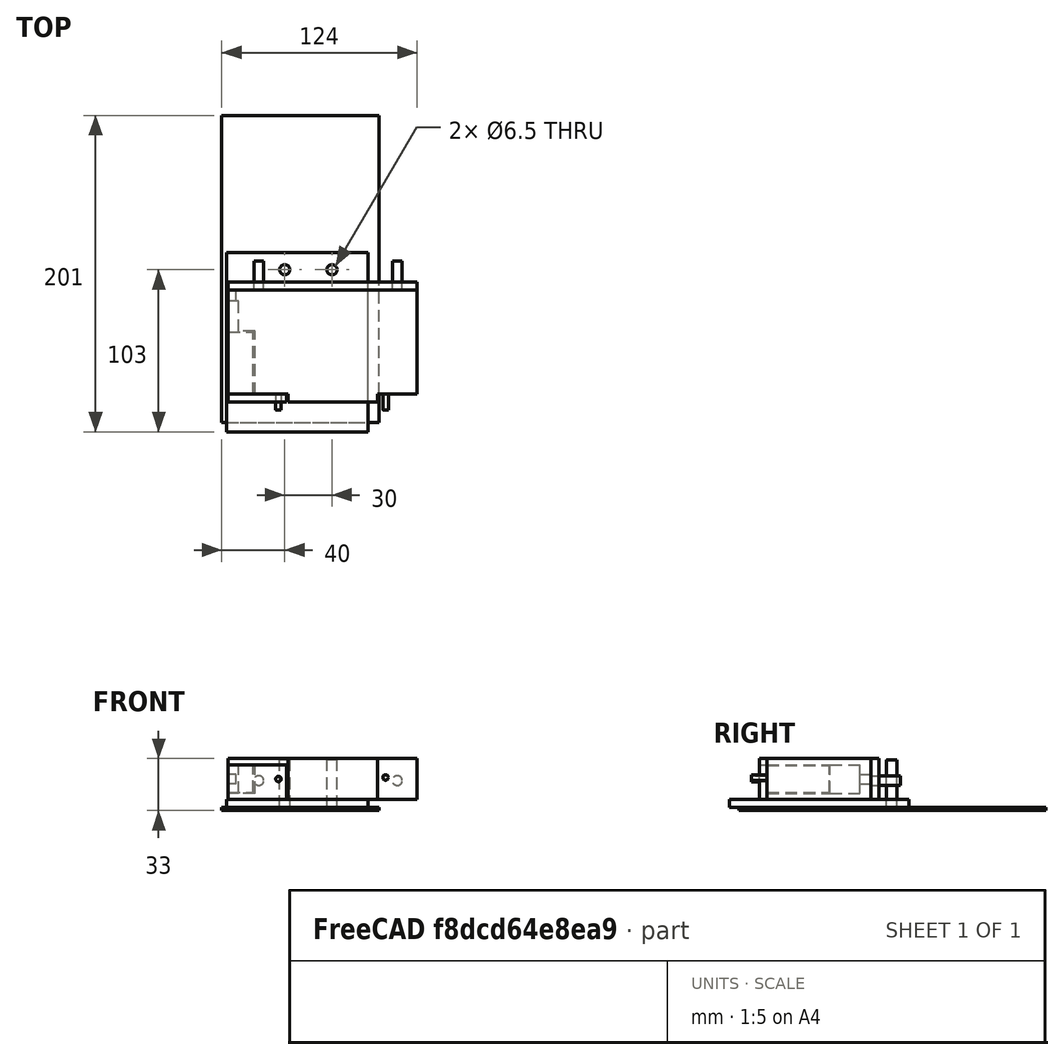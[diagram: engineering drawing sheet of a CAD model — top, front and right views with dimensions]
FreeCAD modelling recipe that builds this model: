
FCSTD DOCUMENT  (FreeCAD 0.18R4 (GitTag))
Label: BreakerHolder
License: All rights reserved
LicenseURL: http://en.wikipedia.org/wiki/All_rights_reserved
objects: Part::Box×10, Part::Cylinder×8, Part::Cut×3, Part::MultiFuse×3
note: 24 computed .brp shape members not serialized (recipe doc carries the construction recipe); baked Part::Feature solids carry a one-line shape summary decoded from their .brp

FEATURE [Part::Box] Box  label="Wall"
  AttacherType = Attacher::AttachEngine3D
  Height = 2
  Length = 100
  Width = 195
FEATURE [Part::Cylinder] Cylinder  label="ScrewHole0"
  Angle = 360
  AttacherType = Attacher::AttachEngine3D
  Height = 10
  Placement = pos=(70,97,-4) rot=(0,0,1;0rad)
  Radius = 3.25
FEATURE [Part::Cylinder] Cylinder001  label="ScrewHole1"
  Angle = 360
  AttacherType = Attacher::AttachEngine3D
  Height = 10
  Placement = pos=(40,97,-3) rot=(0,0,1;0rad)
  Radius = 3.25
FEATURE [Part::Cut] Cut
  Base = -> Box
  Tool = -> Cylinder
FEATURE [Part::Cut] Cut001  label="Wall001"
  Base = -> Cut
  Placement = pos=(154,0,-29) rot=(0,0,1;0rad)
  Tool = -> Cylinder001
FEATURE [Part::Box] Box001  label="Cube"
  AttacherType = Attacher::AttachEngine3D
  Height = 26
  Length = 66
  Width = 120
FEATURE [Part::Cylinder] Cylinder002  label="Cylinder"
  Angle = 360
  AttacherType = Attacher::AttachEngine3D
  Height = 18.5
  Placement = pos=(66,12.5,12) rot=(0,-1,0;4.71239rad)
  Radius = 3.125
FEATURE [Part::Cylinder] Cylinder003  label="Cylinder001"
  Angle = 360
  AttacherType = Attacher::AttachEngine3D
  Height = 18.5
  Placement = pos=(66,100.5,12) rot=(0,1,0;1.5708rad)
  Radius = 3.125
FEATURE [Part::Box] Box002  label="Cube001"
  AttacherType = Attacher::AttachEngine3D
  Height = 26
  Length = 5.6
  Placement = pos=(-5,25,0) rot=(0,0,1;0rad)
  Width = 57
FEATURE [Part::Box] Box003  label="Cube002"
  AttacherType = Attacher::AttachEngine3D
  Height = 6
  Length = 7
  Placement = pos=(59,115,10) rot=(0,0,1;0rad)
  Width = 5
FEATURE [Part::Box] Box004  label="Cube003"
  AttacherType = Attacher::AttachEngine3D
  Height = 18
  Length = 19
  Placement = pos=(40,113.5,4) rot=(0,0,1;0rad)
  Width = 6.5
FEATURE [Part::Box] Box005  label="Cube004"
  AttacherType = Attacher::AttachEngine3D
  Height = 18
  Length = 40
  Placement = pos=(0,103,4) rot=(0,0,1;0rad)
  Width = 17
FEATURE [Part::MultiFuse] Fusion001
  Shapes = -> [Box003,Box005,Box004]
FEATURE [Part::Cylinder] Cylinder004  label="Screw1"
  Angle = 360
  AttacherType = Attacher::AttachEngine3D
  Height = 10
  Placement = pos=(-9e-16,88,13) rot=(0,1,0;4.71239rad)
  Radius = 1.75
FEATURE [Part::Cylinder] Cylinder005  label="Screw2"
  Angle = 360
  AttacherType = Attacher::AttachEngine3D
  Height = 10
  Placement = pos=(-3.1e-15,20,14) rot=(0,1,0;4.71239rad)
  Radius = 1.75
FEATURE [Part::MultiFuse] Fusion
  Shapes = -> [Box002,Cylinder002,Box001,Cylinder003]
FEATURE [Part::Cut] Cut002
  Base = -> Fusion
  Tool = -> Fusion001
FEATURE [Part::MultiFuse] Fusion002
  Placement = pos=(278,18,-22) rot=(0,0,-1;4.71239rad)
  Shapes = -> [Cut002,Cylinder005,Cylinder004]
FEATURE [Part::Cylinder] Cylinder006  label="ScrewHole002"
  Angle = 360
  AttacherType = Attacher::AttachEngine3D
  Height = 30
  Placement = pos=(224,97,-27) rot=(0,0,1;0rad)
  Radius = 3.25
FEATURE [Part::Cylinder] Cylinder007  label="ScrewHole003"
  Angle = 360
  AttacherType = Attacher::AttachEngine3D
  Height = 30
  Placement = pos=(194,97,-27) rot=(0,0,1;0rad)
  Radius = 3.25
FEATURE [Part::Box] Box006  label="Cube005"
  AttacherType = Attacher::AttachEngine3D
  Height = 17
  Length = 16
  Placement = pos=(158,18,-17.5) rot=(0,0,1;0rad)
  Width = 39.5
FEATURE [Part::Box] Box008  label="Cube007"
  AttacherType = Attacher::AttachEngine3D
  Height = 26
  Length = 120
  Placement = pos=(158,84,-22) rot=(0,0,1;0rad)
  Width = 5
FEATURE [Part::Box] Box009  label="Cube008"
  AttacherType = Attacher::AttachEngine3D
  Height = 114
  Length = 90
  Placement = pos=(157,-6,-22) rot=(1,0,0;4.71239rad)
  Width = 5
FEATURE [Part::Box] Box010  label="Cube009"
  AttacherType = Attacher::AttachEngine3D
  Height = 22
  Length = 37
  Placement = pos=(158,13,-22) rot=(0,0,1;0rad)
  Width = 5
